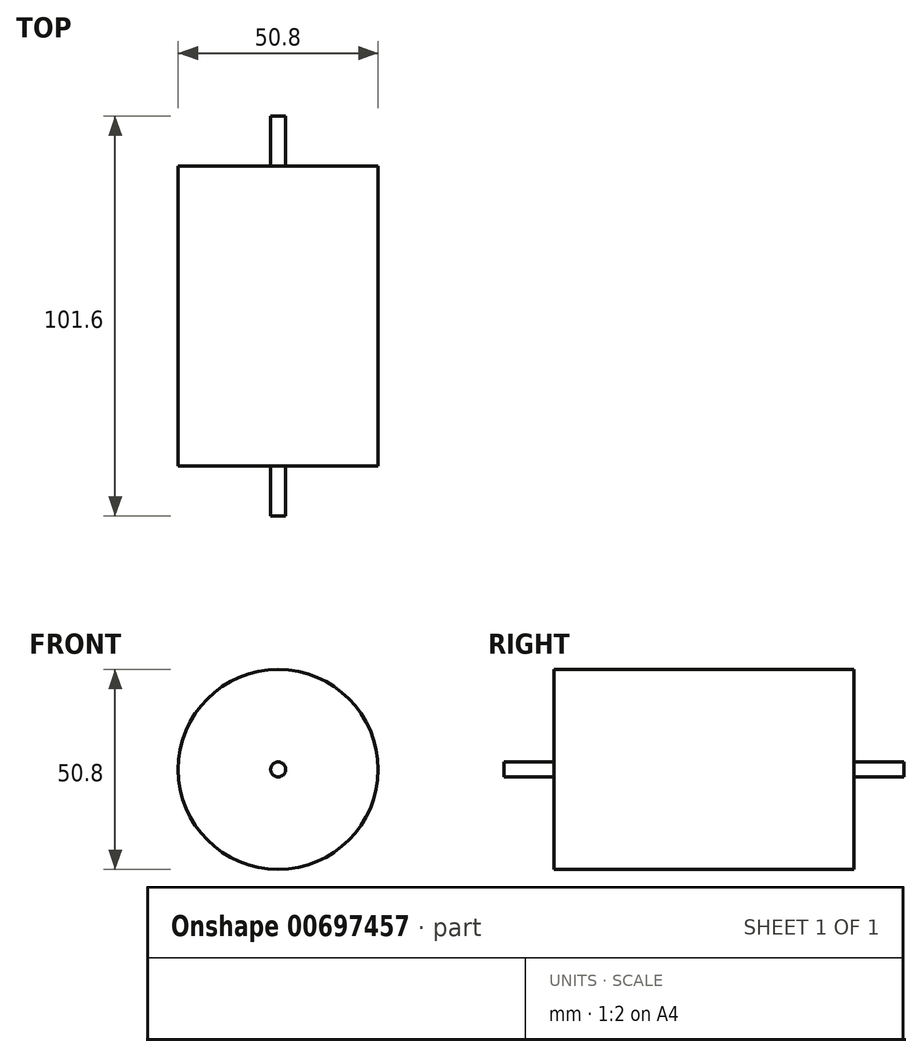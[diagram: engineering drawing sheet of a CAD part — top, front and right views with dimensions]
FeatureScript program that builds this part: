
annotation { "Feature Type Name" : "Feature", "Feature Type Description" : "" }
export const myFeature = defineFeature(function(context is Context, id is Id, definition is map)
    precondition{}
    {
        {
            var Q0;
            Q0=qCreatedBy(makeId("Front.planeOp"),FACE);
            var sketch = newSketch(context, id + "F0", { "sketchPlane" : qUnion([Q0])});
            skCircle(sketch, "E0", {"center": v(0, 0) * mm, "radius": 25.4 * mm});
            skSolve(sketch);
        }
        {
            var Q0;
            Q0 = qSketchRegion(id + "F0", true);
            extrude(context, id + "F1", {"entities" : qUnion([Q0]), "depth" : 38.1 * mm, "offsetDistance" : 25.4 * mm});
        }
        {
            var Q0;
            Q0=makeQuery(id+"F1.opExtrude","CAP_FACE",FACE,{"disambiguationData":[OSD([sQuery(id+"F0.wireOp",EDGE,"E0")])],"isStart":true});
            extrude(context, id + "F2", {"entities" : qUnion([Q0]), "operationType" : NewBodyOperationType.ADD, "depth" : 38.1 * mm, "offsetDistance" : 25.4 * mm});
        }
        {
            var Q0;
            Q0=makeQuery(id+"F1.opExtrude","CAP_FACE",FACE,{"disambiguationData":[OSD([sQuery(id+"F0.wireOp",EDGE,"E0")])],"isStart":false});
            var sketch = newSketch(context, id + "F3", { "sketchPlane" : qUnion([Q0])});
            skCircle(sketch, "E1", {"center": v(0, 0) * mm, "radius": 1.9 * mm});
            skSolve(sketch);
        }
        {
            var Q0;
            Q0=makeQuery(id+"F2.opExtrude","CAP_FACE",FACE,{"disambiguationData":[OSD([sQuery(id+"F0.wireOp",EDGE,"E0")])],"isStart":false});
            var sketch = newSketch(context, id + "F4", { "sketchPlane" : qUnion([Q0])});
            skCircle(sketch, "E2", {"center": v(0, 0) * mm, "radius": 1.9 * mm});
            skSolve(sketch);
        }
        {
            var Q0;
            Q0=makeQuery(id+"F4.imprint","IMPRINT",FACE,{"disambiguationData":[TD([[makeQuery(id+"F4.imprint","IMPRINT",EDGE,{"derivedFrom":sQuery(id+"F4.wireOp",EDGE,"E2")}),1.0]])]});
            extrude(context, id + "F5", {"entities" : qUnion([Q0]), "operationType" : NewBodyOperationType.ADD, "depth" : 12.7 * mm, "offsetDistance" : 25.4 * mm});
        }
        {
            var Q0;
            Q0=makeQuery(id+"F3.imprint","IMPRINT",FACE,{"disambiguationData":[TD([[makeQuery(id+"F3.imprint","IMPRINT",EDGE,{"derivedFrom":sQuery(id+"F3.wireOp",EDGE,"E1")}),1.0]])]});
            extrude(context, id + "F6", {"entities" : qUnion([Q0]), "operationType" : NewBodyOperationType.ADD, "depth" : 12.7 * mm, "offsetDistance" : 25.4 * mm});
        }
    });
